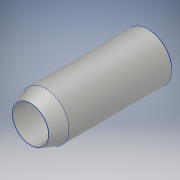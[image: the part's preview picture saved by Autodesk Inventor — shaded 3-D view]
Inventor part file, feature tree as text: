
AUTODESK INVENTOR PART (.ipt)
format: ipt  version: 2019 (Build 230136000, 136)  size: 118,272 bytes
history: native  units: mm
features: other x1, chamfer x1, sketch x1
ambient origin geometry x8: Origin, YZ Plane, XZ Plane, XY Plane, X Axis, Y Axis, Z Axis, Center Point
bodies: Solide1 (feature_tree)
feature tree (3):
  other  "Révolution1"
  chamfer  "Chanfrein1"  Distance=27.925268mm
  sketch  "Esquisse1"
